# Revit family: 13_CMP_FD201-50_F1A+FL-DX
name_source: partatom
category: Finestre
units: mm (PartAtom-declared; Revit-internal decimal feet)

## family parameters
Condiviso = No
Host = Muro
Numero OmniClass = 23.30.20.00
Punto di calcolo locali = Sì
Sempre verticale = Sì
Taglio con vuoti quando caricato = No
Titolo OmniClass = Windows

## types (3) — shared parameters
Altezza di default del davanzale = 800 mm  [stored 2.62467 ft]
Chiusura muro = Per host
Codice assieme = B2020100
Coefficiente di scambio termico (U) = 1 W/(m²·K)
Costruzione analitica = <Nessuno>
EXTERNAL ALUMINUM FRAME/TELAIO ALLUMINIO ESTERNO = UNIFORM_ALUMINUM
HANDLE/MANIGLIA = UNIFORM_ALUMINUM
INTERIOR WOOD FRAME/TELAIO LEGNO INTERNO = UNIFORM_WOOD
Immagine tipo = <Nessuno>
MAXIMUM HEIGHT/ALTEZZA MASSIMA = 1800 mm  [stored 5.90551 ft]
MAXIMUM WIDTH/LARGHEZZA MASSIMA = 2000 mm  [stored 6.56168 ft]
MINIMUM HEIGHT/ALTEZZA MINIMA = 800 mm  [stored 2.62467 ft]
MINIMUM WIDTH/LARGHEZZA MINIMA  = 800 mm  [stored 2.62467 ft]
Modello = COMPLANARE
PRODUCER WEBSITE/SITO WEB PRODUTTORE = www.uniform.it
PRODUCT WEBSITE/SITO WEB PRODOTTO = www.sistema-uni-one.it
Produttore = UNIFORM
Resistenza termica (R) = 0.0000 (m²·K)/W
URL = https://www.sistema-uni-one.it
WINDOW GLASS/VETRO FINESTRA = UNIFORM_GLASS
WINDOW SILL/BANCALINO FINESTRA = UNIFORM_STONE
zero-valued in all types: Indice di riscaldamento alla radiazione solare, Trasmittanza luminosa

## per-type parameters (varying)
| type | Altezza | GLASS WEIGHT/PESO VETRO | H | HANDLE HEIGHT/ALTEZZA MANIGLIA | HOLE_H | HOLE_W | Larghezza | MAX_DIMENSIONS_WARNING | Rw GLASS/Rw VETRO | Rw WINDOW/Rw FINESTRA | T_F_H | Ug GLASS/Ug VETRO | Uw WINDOW/Uw FINESTRA | W | W/2 | WINDOW HOLE TOLERANCE/TOLLERANZA FORO FINESTRA |
| F1A+FL-DX_HIGH THERMAL PERFORMANCE | 2000 mm  [stored 6.56168 ft] | 43.00 kg/m² | 1770 mm | 540 mm | 1800 mm  [stored 5.90551 ft] | 2000 mm  [stored 6.56168 ft] | 3000 mm  [stored 9.84252 ft] | Sì | 0 | 0 | 30 mm  [stored 0.0984252 ft] | 0.5 W/(m²·K) | 0.8 W/(m²·K) | 1940 mm  [stored 6.36483 ft] | 985 mm | 200 mm  [stored 0.656168 ft] |
| F1A+FL-DX_ACOUSTICS | 1600 mm  [stored 5.24934 ft] | 60.00 kg/m² | 1600 mm  [stored 5.24934 ft] | 800 mm  [stored 2.62467 ft] | 1600 mm  [stored 5.24934 ft] | 1400 mm  [stored 4.59318 ft] | 1400 mm  [stored 4.59318 ft] | No | 49 | 43 | 0 mm  [stored 0 ft] | 1.1 W/(m²·K) | 1.3 W/(m²·K) | 1400 mm  [stored 4.59318 ft] | 715 mm  [stored 2.3458 ft] | 0 mm  [stored 0 ft] |
| F1A+FL-DX_THERMAL | 2000 mm  [stored 6.56168 ft] | 43.00 kg/m² | 1770 mm | 500 mm  [stored 1.64042 ft] | 1800 mm  [stored 5.90551 ft] | 2000 mm  [stored 6.56168 ft] | 3000 mm  [stored 9.84252 ft] | Sì | 0 | 0 | 30 mm  [stored 0.0984252 ft] | 1 W/(m²·K) | 1.2 W/(m²·K) | 1940 mm  [stored 6.36483 ft] | 985 mm | 50 mm  [stored 0.164042 ft] |

note: [stored X ft] marks values corroborated as IEEE doubles in the binary element streams (Revit-internal decimal feet)
